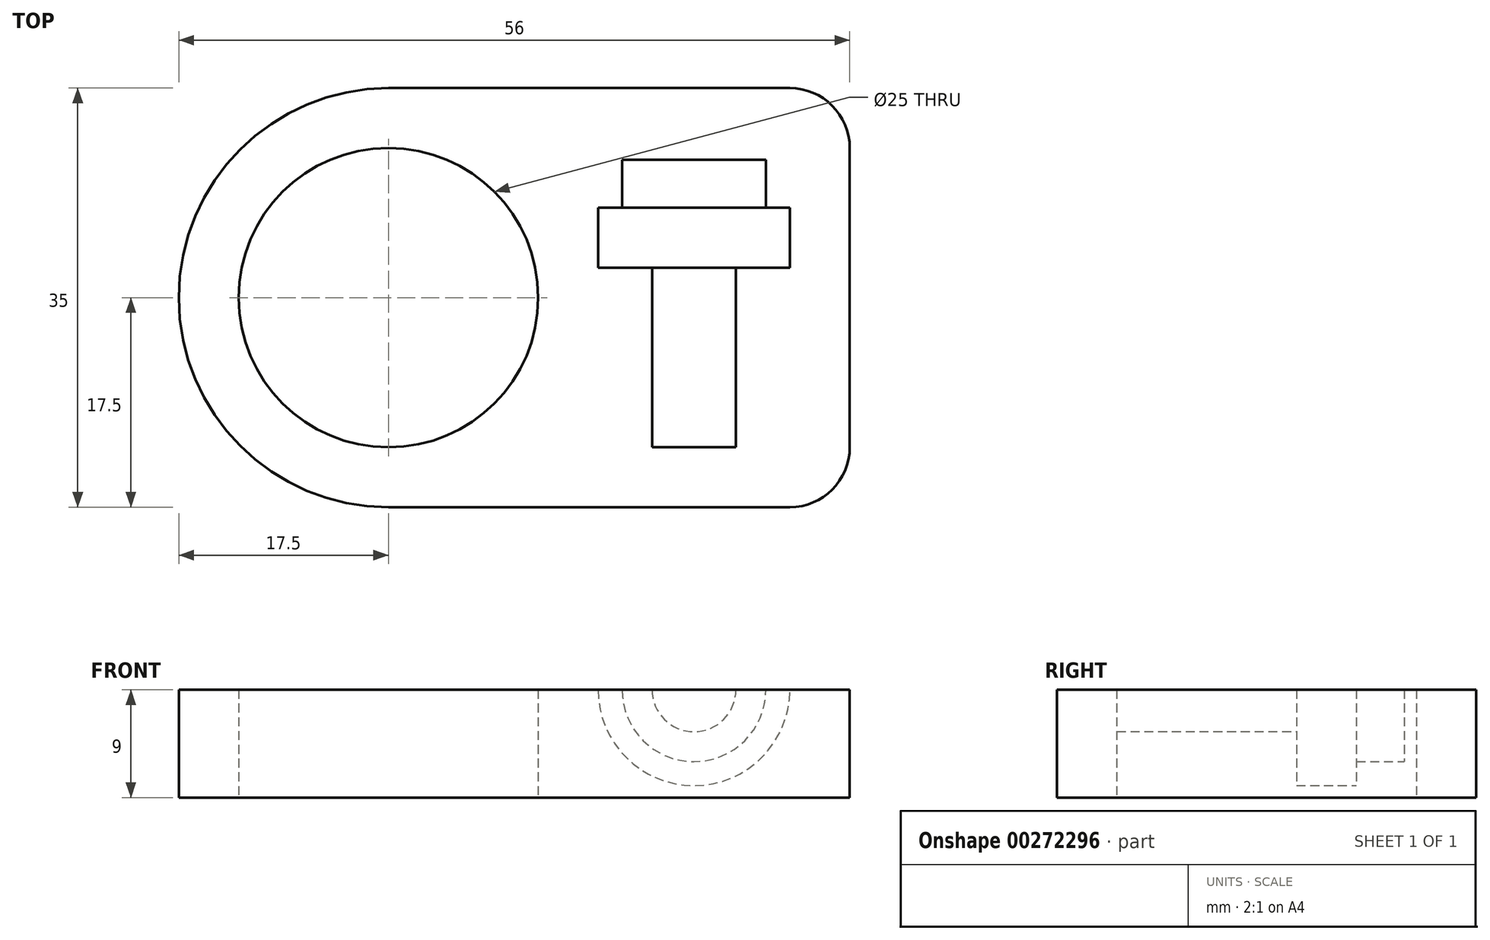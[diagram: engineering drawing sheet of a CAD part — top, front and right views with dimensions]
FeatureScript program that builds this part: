
annotation { "Feature Type Name" : "Feature", "Feature Type Description" : "" }
export const myFeature = defineFeature(function(context is Context, id is Id, definition is map)
    precondition{}
    {
        {
            var Q0;
            Q0=qCreatedBy(makeId("Top.planeOp"),FACE);
            var sketch = newSketch(context, id + "F0", { "sketchPlane" : qUnion([Q0])});
            skLineSegment(sketch, "E0.bottom", {"start": v(17.5, 0) * mm, "end": v(51, 0) * mm});
            skLineSegment(sketch, "E0.top", {"start": v(17.5, 35) * mm, "end": v(51, 35) * mm});
            skLineSegment(sketch, "E0.left", {"start": v(0, 17.5) * mm, "end": v(0, 17.5) * mm});
            skLineSegment(sketch, "E0.right", {"start": v(56, 5) * mm, "end": v(56, 30) * mm});
            skLineSegment(sketch, "E1.bottom", {"start": v(0, 0) * mm, "end": v(17.5, 0) * mm, "construction": true});
            skLineSegment(sketch, "E1.top", {"start": v(0, 17.5) * mm, "end": v(17.5, 17.5) * mm, "construction": true});
            skLineSegment(sketch, "E1.left", {"start": v(0, 0) * mm, "end": v(0, 17.5) * mm, "construction": true});
            skLineSegment(sketch, "E1.right", {"start": v(17.5, 0) * mm, "end": v(17.5, 17.5) * mm, "construction": true});
            skCircle(sketch, "E2", {"center": v(17.5, 17.5) * mm, "radius": 12.5 * mm});
            skPoint(sketch, "E3.visualSharp", {"position": v(0, 0) * mm});
            skArc(sketch, "E3.filletArc", {"start": v(0, 17.5) * mm, "mid": v(5.13, 5.13) * mm, "end": v(17.5, 0) * mm});
            skPoint(sketch, "E4.visualSharp", {"position": v(0, 35) * mm});
            skArc(sketch, "E4.filletArc", {"start": v(17.5, 35) * mm, "mid": v(5.13, 29.87) * mm, "end": v(0, 17.5) * mm});
            skPoint(sketch, "E5.visualSharp", {"position": v(56, 35) * mm});
            skArc(sketch, "E5.filletArc", {"start": v(56, 30) * mm, "mid": v(54.54, 33.54) * mm, "end": v(51, 35) * mm});
            skPoint(sketch, "E6.visualSharp", {"position": v(56, 0) * mm});
            skArc(sketch, "E6.filletArc", {"start": v(51, 0) * mm, "mid": v(54.54, 1.46) * mm, "end": v(56, 5) * mm});
            skSolve(sketch);
        }
        {
            var Q0;
            Q0=makeQuery(id+"F0.imprint","IMPRINT",FACE,{"disambiguationData":[TD([[makeQuery(id+"F0.imprint","IMPRINT",EDGE,{"derivedFrom":sQuery(id+"F0.wireOp",EDGE,"E0.bottom")}),1.0]])]});
            extrude(context, id + "F1", {"entities" : qUnion([Q0]), "depth" : 9 * mm});
        }
        {
            var Q0;
            Q0=makeQuery(id+"F1.opExtrude","CAP_FACE",FACE,{"disambiguationData":[OSD([sQuery(id+"F0.wireOp",EDGE,"E0.bottom"),sQuery(id+"F0.wireOp",EDGE,"E0.top"),sQuery(id+"F0.wireOp",EDGE,"E0.right"),sQuery(id+"F0.wireOp",EDGE,"E2"),sQuery(id+"F0.wireOp",EDGE,"E3.filletArc"),sQuery(id+"F0.wireOp",EDGE,"E4.filletArc"),sQuery(id+"F0.wireOp",EDGE,"E5.filletArc"),sQuery(id+"F0.wireOp",EDGE,"E6.filletArc")])],"isStart":false});
            var sketch = newSketch(context, id + "F2", { "sketchPlane" : qUnion([Q0])});
            skLineSegment(sketch, "E7.bottom", {"start": v(0, 0) * mm, "end": v(43, 0) * mm, "construction": true});
            skLineSegment(sketch, "E7.top", {"start": v(0, 5) * mm, "end": v(43, 5) * mm, "construction": true});
            skLineSegment(sketch, "E7.left", {"start": v(0, 0) * mm, "end": v(0, 5) * mm, "construction": true});
            skLineSegment(sketch, "E7.right", {"start": v(43, 0) * mm, "end": v(43, 5) * mm, "construction": true});
            skLineSegment(sketch, "E8.bottom", {"start": v(43, 5) * mm, "end": v(46.5, 5) * mm});
            skLineSegment(sketch, "E8.left", {"start": v(43, 5) * mm, "end": v(43, 20) * mm});
            skLineSegment(sketch, "E8.right", {"start": v(46.5, 5) * mm, "end": v(46.5, 20) * mm});
            skLineSegment(sketch, "E9.bottom", {"start": v(46.5, 20) * mm, "end": v(51, 20) * mm});
            skLineSegment(sketch, "E9.top", {"start": v(49, 25) * mm, "end": v(51, 25) * mm});
            skLineSegment(sketch, "E9.left", {"start": v(43, 20) * mm, "end": v(43, 25) * mm});
            skLineSegment(sketch, "E9.right", {"start": v(51, 20) * mm, "end": v(51, 25) * mm});
            skLineSegment(sketch, "E10.top", {"start": v(43, 29) * mm, "end": v(49, 29) * mm});
            skLineSegment(sketch, "E10.left", {"start": v(43, 25) * mm, "end": v(43, 29) * mm});
            skLineSegment(sketch, "E10.right", {"start": v(49, 25) * mm, "end": v(49, 29) * mm});
            skSolve(sketch);
        }
        {
            var Q0;
            Q0=makeQuery(id+"F2.imprint","IMPRINT",FACE,{"disambiguationData":[TD([[makeQuery(id+"F2.imprint","IMPRINT",EDGE,{"derivedFrom":sQuery(id+"F2.wireOp",EDGE,"E8.bottom")}),1.0]])]});
            var Q1;
            Q1=sQuery(id+"F2.wireOp",EDGE,"E8.left");
            revolve(context, id + "F3", {"operationType" : NewBodyOperationType.REMOVE, "entities" : qUnion([Q0]), "axis" : qUnion([Q1]), "revolveType" : RevolveType.FULL, "oppositeDirection" : true});
        }
    });
